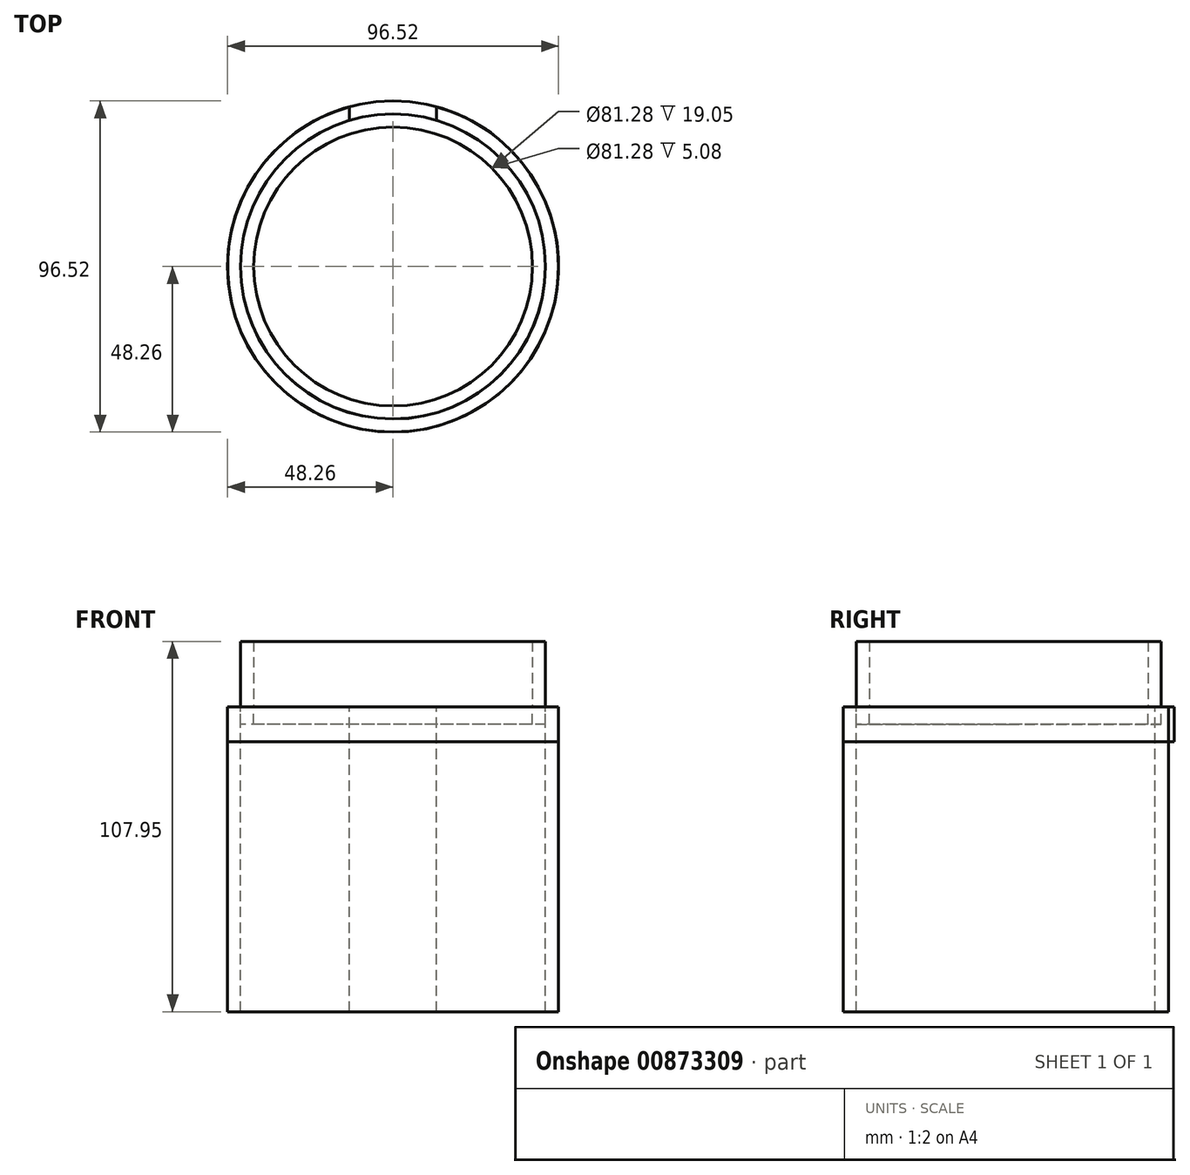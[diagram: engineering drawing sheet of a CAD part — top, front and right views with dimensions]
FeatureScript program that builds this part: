
annotation { "Feature Type Name" : "Feature", "Feature Type Description" : "" }
export const myFeature = defineFeature(function(context is Context, id is Id, definition is map)
    precondition{}
    {
        {
            var Q0;
            Q0=qCreatedBy(makeId("Top.planeOp"),FACE);
            var sketch = newSketch(context, id + "F0", { "sketchPlane" : qUnion([Q0])});
            skCircle(sketch, "E0", {"center": v(0, 0) * mm, "radius": 31.75 * mm});
            skCircle(sketch, "E1", {"center": v(0, 0) * mm, "radius": 30.48 * mm});
            skPoint(sketch, "E2", {"position": v(-12.7, 46.56) * mm});
            skPoint(sketch, "E3", {"position": v(12.7, 46.56) * mm});
            skPoint(sketch, "E4", {"position": v(12.7, 42.6) * mm});
            skPoint(sketch, "E5", {"position": v(-12.7, 42.6) * mm});
            skLineSegment(sketch, "E6", {"start": v(-12.7, 42.6) * mm, "end": v(-12.7, 42.6) * mm});
            skLineSegment(sketch, "E7", {"start": v(12.7, 46.56) * mm, "end": v(0, 46.56) * mm});
            skArc(sketch, "E8", {"start": v(-12.7, 46.56) * mm, "mid": v(0, -48.26) * mm, "end": v(12.7, 46.56) * mm});
            skArc(sketch, "E9", {"start": v(-12.7, 42.6) * mm, "mid": v(0, -44.45) * mm, "end": v(12.7, 42.6) * mm});
            skLineSegment(sketch, "E10", {"start": v(12.7, 42.6) * mm, "end": v(12.7, 42.6) * mm});
            skLineSegment(sketch, "E11", {"start": v(-12.7, 42.6) * mm, "end": v(0, 42.6) * mm});
            skLineSegment(sketch, "E12", {"start": v(-12.7, 46.56) * mm, "end": v(-12.7, 42.6) * mm});
            skLineSegment(sketch, "E13", {"start": v(12.7, 46.56) * mm, "end": v(12.7, 42.6) * mm});
            skPoint(sketch, "E14", {"position": v(0, 46.56) * mm});
            skPoint(sketch, "E15", {"position": v(0, 42.6) * mm});
            skLineSegment(sketch, "E16", {"start": v(0, 46.56) * mm, "end": v(-12.7, 46.56) * mm});
            skLineSegment(sketch, "E17", {"start": v(0, 42.6) * mm, "end": v(12.7, 42.6) * mm});
            skSolve(sketch);
        }
        {
            var Q0;
            Q0=makeQuery(id+"F0.imprint","IMPRINT",FACE,{"disambiguationData":[TD([[makeQuery(id+"F0.imprint","IMPRINT",EDGE,{"derivedFrom":sQuery(id+"F0.wireOp",EDGE,"7YdN1t4v-y8Iu-WTfN-s7mx-nHIzf7sdSsJH")}),1.0]])]});
            var Q1;
            Q1=makeQuery(id+"F0.imprint","IMPRINT",FACE,{"disambiguationData":[TD([[makeQuery(id+"F0.imprint","IMPRINT",EDGE,{"derivedFrom":sQuery(id+"F0.wireOp",EDGE,"E8")}),1.0]])]});
            extrude(context, id + "F1", {"entities" : qUnion([Q0, Q1]), "depth" : -88.9 * mm, "offsetDistance" : 25.4 * mm});
        }
        {
            var Q0;
            Q0=qCreatedBy(makeId("Top.planeOp"),FACE);
            var sketch = newSketch(context, id + "F2", { "sketchPlane" : qUnion([Q0])});
            skCircle(sketch, "E18", {"center": v(0, 0) * mm, "radius": 30.48 * mm});
            skCircle(sketch, "E19", {"center": v(0, 0) * mm, "radius": 48.26 * mm});
            skSolve(sketch);
        }
        {
            var Q0;
            Q0=makeQuery(id+"F2.imprint","IMPRINT",FACE,{"disambiguationData":[TD([[makeQuery(id+"F2.imprint","IMPRINT",EDGE,{"derivedFrom":sQuery(id+"F2.wireOp",EDGE,"E18")}),-1.0]])]});
            var Q1;
            Q1=makeQuery(id+"F2.imprint","IMPRINT",FACE,{"disambiguationData":[TD([[makeQuery(id+"F2.imprint","IMPRINT",EDGE,{"derivedFrom":sQuery(id+"F2.wireOp",EDGE,"E18")}),1.0]])]});
            extrude(context, id + "F3", {"entities" : qUnion([Q0, Q1]), "depth" : -10.16 * mm, "offsetDistance" : 25.4 * mm});
        }
        {
            var Q0;
            Q0=qCreatedBy(makeId("Top.planeOp"),FACE);
            var sketch = newSketch(context, id + "F4", { "sketchPlane" : qUnion([Q0])});
            skCircle(sketch, "E20", {"center": v(0, 0) * mm, "radius": 44.45 * mm});
            skCircle(sketch, "E21", {"center": v(0, 0) * mm, "radius": 40.64 * mm});
            skSolve(sketch);
        }
        {
            var Q0;
            Q0=makeQuery(id+"F4.imprint","IMPRINT",FACE,{"disambiguationData":[TD([[makeQuery(id+"F4.imprint","IMPRINT",EDGE,{"derivedFrom":sQuery(id+"F4.wireOp",EDGE,"E20")}),1.0]])]});
            extrude(context, id + "F5", {"entities" : qUnion([Q0]), "depth" : 19.05 * mm, "offsetDistance" : 25.4 * mm});
        }
        {
            var Q0;
            Q0 = qSketchRegion(id + "F4", true);
            extrude(context, id + "F6", {"entities" : qUnion([Q0]), "depth" : -5.08 * mm, "offsetDistance" : 25.4 * mm});
        }
    });
